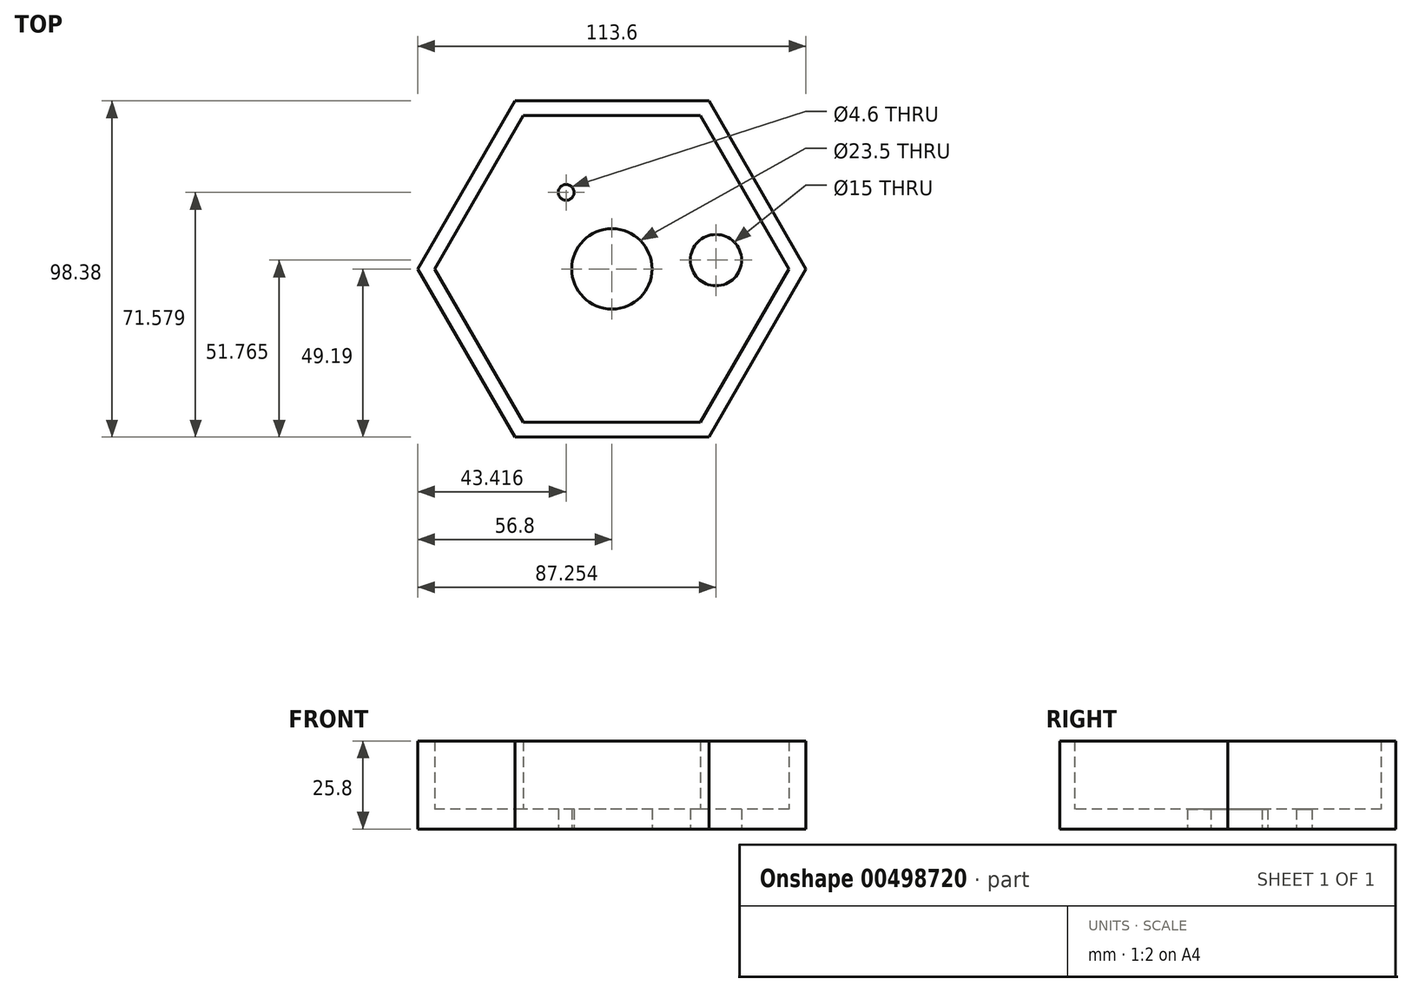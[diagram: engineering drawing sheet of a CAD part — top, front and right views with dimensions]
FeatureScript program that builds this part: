
annotation { "Feature Type Name" : "Feature", "Feature Type Description" : "" }
export const myFeature = defineFeature(function(context is Context, id is Id, definition is map)
    precondition{}
    {
        {
            var Q0;
            Q0=qCreatedBy(makeId("Top.planeOp"),FACE);
            var sketch = newSketch(context, id + "F0", { "sketchPlane" : qUnion([Q0])});
            skLineSegment(sketch, "E0", {"start": v(-25.9, 44.86) * mm, "end": v(-51.8, 0) * mm});
            skLineSegment(sketch, "E1", {"start": v(25.9, 44.86) * mm, "end": v(51.8, 0) * mm});
            skLineSegment(sketch, "E2", {"start": v(-51.8, 0) * mm, "end": v(-25.9, -44.86) * mm});
            skLineSegment(sketch, "E3", {"start": v(51.8, 0) * mm, "end": v(25.9, -44.86) * mm});
            skLineSegment(sketch, "E4", {"start": v(25.9, -44.86) * mm, "end": v(-25.9, -44.86) * mm});
            skCircle(sketch, "E5", {"center": v(0, 0) * mm, "radius": 44.86 * mm, "construction": true});
            skLineSegment(sketch, "E6", {"start": v(-25.9, 44.86) * mm, "end": v(25.9, 44.86) * mm});
            skCircle(sketch, "E7", {"center": v(0, 0) * mm, "radius": 11.75 * mm});
            skCircle(sketch, "E8", {"center": v(-13.38, 22.39) * mm, "radius": 2.3 * mm});
            skCircle(sketch, "E9", {"center": v(30.45, 2.58) * mm, "radius": 7.5 * mm});
            skLineSegment(sketch, "E10", {"start": v(-28.4, 49.2) * mm, "end": v(-56.8, 0) * mm});
            skLineSegment(sketch, "E11", {"start": v(28.4, 49.2) * mm, "end": v(56.8, 0) * mm});
            skLineSegment(sketch, "E12", {"start": v(-56.8, 0) * mm, "end": v(-28.4, -49.2) * mm});
            skLineSegment(sketch, "E13", {"start": v(56.8, 0) * mm, "end": v(28.4, -49.2) * mm});
            skLineSegment(sketch, "E14", {"start": v(28.4, -49.2) * mm, "end": v(-28.4, -49.2) * mm});
            skCircle(sketch, "E15", {"center": v(0, 0) * mm, "radius": 49.2 * mm, "construction": true});
            skLineSegment(sketch, "E16", {"start": v(-28.4, 49.2) * mm, "end": v(28.4, 49.2) * mm});
            skSolve(sketch);
        }
        {
            var Q0;
            Q0=makeQuery(id+"F0.imprint","IMPRINT",FACE,{"disambiguationData":[TD([[makeQuery(id+"F0.imprint","IMPRINT",EDGE,{"derivedFrom":sQuery(id+"F0.wireOp",EDGE,"E0")}),1.0]])]});
            extrude(context, id + "F1", {"entities" : qUnion([Q0]), "depth" : 5.8 * mm});
        }
        {
            var Q0;
            Q0=makeQuery(id+"F0.imprint","IMPRINT",FACE,{"disambiguationData":[TD([[makeQuery(id+"F0.imprint","IMPRINT",EDGE,{"derivedFrom":sQuery(id+"F0.wireOp",EDGE,"E0")}),-1.0]])]});
            extrude(context, id + "F2", {"entities" : qUnion([Q0]), "operationType" : NewBodyOperationType.ADD, "depth" : 25.8 * mm});
        }
    });
